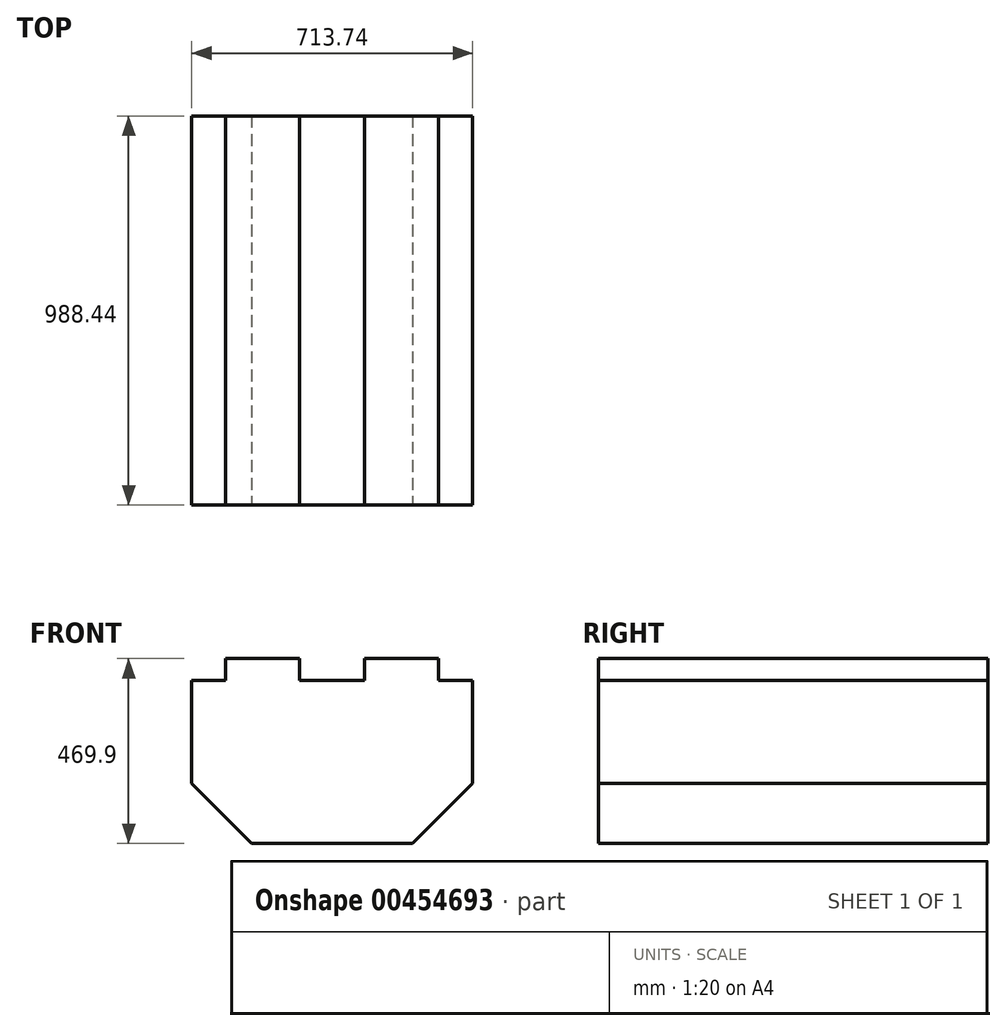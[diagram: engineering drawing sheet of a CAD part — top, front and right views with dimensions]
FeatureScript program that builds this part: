
annotation { "Feature Type Name" : "Feature", "Feature Type Description" : "" }
export const myFeature = defineFeature(function(context is Context, id is Id, definition is map)
    precondition{}
    {
        {
            var Q0;
            Q0=qCreatedBy(makeId("Front.planeOp"),FACE);
            var sketch = newSketch(context, id + "F0", { "sketchPlane" : qUnion([Q0])});
            skLineSegment(sketch, "E0", {"start": v(-459.19, -496.16) * mm, "end": v(-459.19, -234.54) * mm});
            skLineSegment(sketch, "E1", {"start": v(-459.19, -234.54) * mm, "end": v(-372.83, -234.54) * mm});
            skLineSegment(sketch, "E2", {"start": v(-372.83, -234.54) * mm, "end": v(-372.83, -178.66) * mm});
            skLineSegment(sketch, "E3", {"start": v(-372.83, -178.66) * mm, "end": v(-184.87, -178.66) * mm});
            skLineSegment(sketch, "E4", {"start": v(-184.87, -178.66) * mm, "end": v(-184.87, -234.54) * mm});
            skLineSegment(sketch, "E5", {"start": v(-184.87, -234.54) * mm, "end": v(-19.77, -234.54) * mm});
            skLineSegment(sketch, "E6", {"start": v(-19.77, -234.54) * mm, "end": v(-19.77, -178.66) * mm});
            skLineSegment(sketch, "E7", {"start": v(-19.77, -178.66) * mm, "end": v(168.2, -178.66) * mm});
            skLineSegment(sketch, "E8", {"start": v(168.2, -178.66) * mm, "end": v(168.2, -234.54) * mm});
            skLineSegment(sketch, "E9", {"start": v(168.2, -234.54) * mm, "end": v(254.55, -234.54) * mm});
            skLineSegment(sketch, "E10", {"start": v(254.55, -234.54) * mm, "end": v(254.55, -496.16) * mm});
            skLineSegment(sketch, "E11", {"start": v(102.15, -648.56) * mm, "end": v(-306.79, -648.56) * mm});
            skPoint(sketch, "E12.visualSharp", {"position": v(-459.19, -648.56) * mm});
            skPoint(sketch, "E13.visualSharp", {"position": v(254.55, -648.56) * mm});
            skLineSegment(sketch, "E14", {"start": v(-459.19, -496.16) * mm, "end": v(-306.79, -648.56) * mm});
            skLineSegment(sketch, "E15", {"start": v(254.55, -496.16) * mm, "end": v(102.15, -648.56) * mm});
            skSolve(sketch);
        }
        {
            var Q0;
            Q0 = qSketchRegion(id + "F0", true);
            extrude(context, id + "F1", {"entities" : qUnion([Q0]), "oppositeDirection" : true, "depth" : 988.44 * mm});
        }
    });
